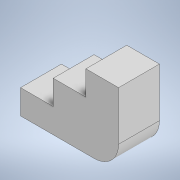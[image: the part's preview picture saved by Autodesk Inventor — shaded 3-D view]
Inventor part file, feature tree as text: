
AUTODESK INVENTOR PART (.ipt)
format: ipt  version: 2022 (Build 260153000, 153)  size: 102,912 bytes
history: native  units: mm
features: other x1, extrude x1, sketch x1
ambient origin geometry x8: Origin, YZ Plane, XZ Plane, XY Plane, X Axis, Y Axis, Z Axis, Center Point
bodies: Body1 (feature_tree)
feature tree (3):
  other  "Sólido1"
  extrude  "Extrusão1"  Depth=15.0mm
  sketch  "Esboço1"  dims[d0=60.0mm d1=15.0mm d2=20.0mm d3=15.0mm d4=20.0mm d5=15.0mm d6=20.0mm d7=15.0mm d8=25.0mm d9=0.0mm]
